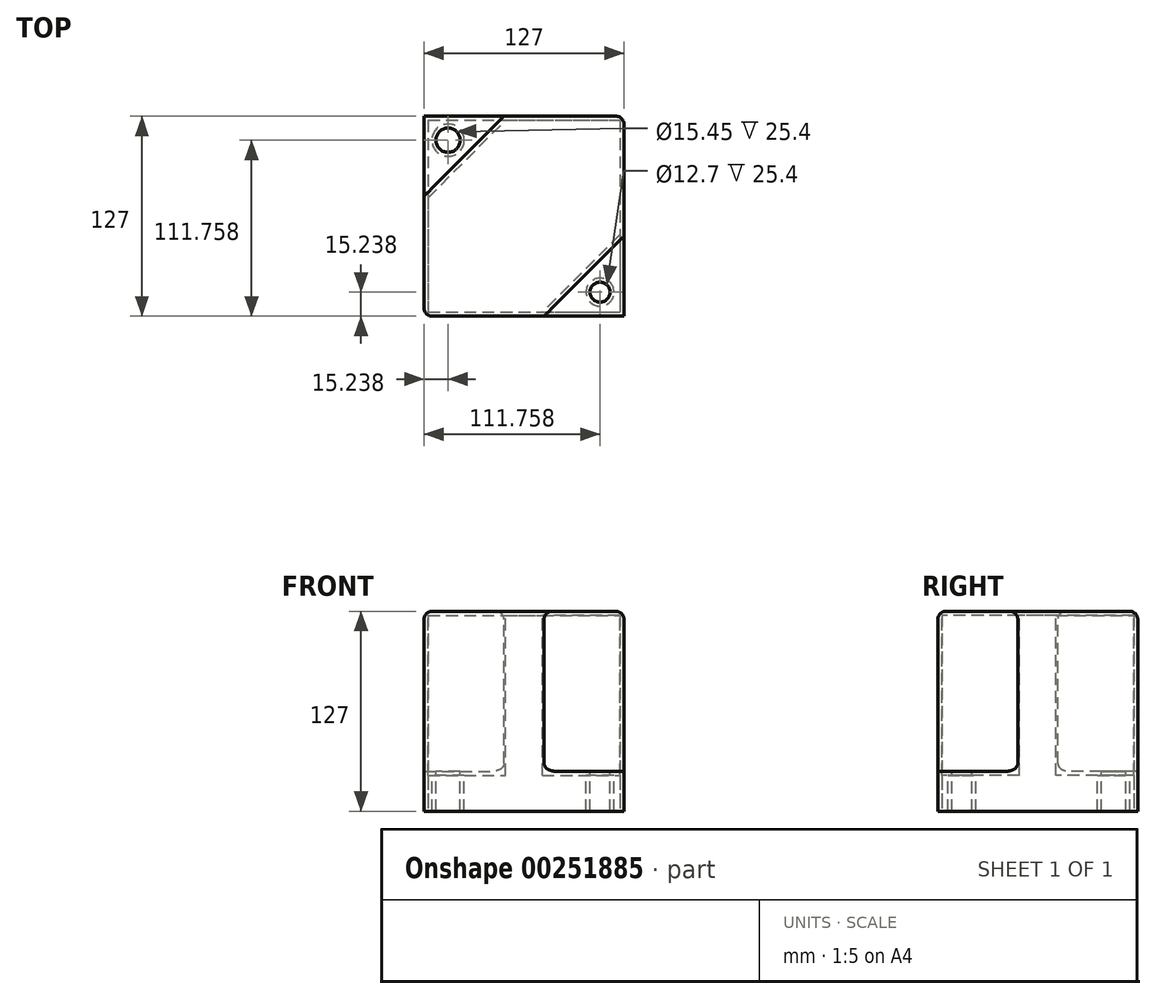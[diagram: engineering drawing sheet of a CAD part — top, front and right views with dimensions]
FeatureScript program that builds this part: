
annotation { "Feature Type Name" : "Feature", "Feature Type Description" : "" }
export const myFeature = defineFeature(function(context is Context, id is Id, definition is map)
    precondition{}
    {
        {
            var Q0;
            Q0=qCreatedBy(makeId("Top.planeOp"),FACE);
            var sketch = newSketch(context, id + "F0", { "sketchPlane" : qUnion([Q0])});
            skLineSegment(sketch, "E0.bottom", {"start": v(-61.38, 68.42) * mm, "end": v(65.62, 68.42) * mm});
            skLineSegment(sketch, "E0.top", {"start": v(-61.38, -58.58) * mm, "end": v(65.62, -58.58) * mm});
            skLineSegment(sketch, "E0.left", {"start": v(-61.38, 68.42) * mm, "end": v(-61.38, -58.58) * mm});
            skLineSegment(sketch, "E0.right", {"start": v(65.62, 68.42) * mm, "end": v(65.62, -58.58) * mm});
            skSolve(sketch);
        }
        {
            var Q0;
            Q0 = qSketchRegion(id + "F0", true);
            extrude(context, id + "F1", {"entities" : qUnion([Q0]), "depth" : 127 * mm});
        }
        {
            var Q0;
            Q0=makeQuery(id+"F1.opExtrude","CAP_FACE",FACE,{"disambiguationData":[OSD([sQuery(id+"F0.wireOp",EDGE,"E0.bottom"),sQuery(id+"F0.wireOp",EDGE,"E0.top"),sQuery(id+"F0.wireOp",EDGE,"E0.left"),sQuery(id+"F0.wireOp",EDGE,"E0.right")])],"isStart":false});
            var sketch = newSketch(context, id + "F2", { "sketchPlane" : qUnion([Q0])});
            skLineSegment(sketch, "E1", {"start": v(-61.38, 17.62) * mm, "end": v(-10.58, 68.42) * mm});
            skLineSegment(sketch, "E2", {"start": v(65.62, -7.78) * mm, "end": v(14.82, -58.58) * mm});
            skSolve(sketch);
        }
        {
            var Q0;
            {var subQ0=sQuery(id+"F2.wireOp",EDGE,"E1");Q0=makeQuery(id+"F2.imprint","IMPRINT",FACE,{"disambiguationData":[TD([[makeQuery(id+"F2.imprint","IMPRINT",EDGE,{"derivedFrom":subQ0}),1.0]])]});}
            var Q1;
            {var subQ0=sQuery(id+"F2.wireOp",EDGE,"E2");Q1=makeQuery(id+"F2.imprint","IMPRINT",FACE,{"disambiguationData":[TD([[makeQuery(id+"F2.imprint","IMPRINT",EDGE,{"derivedFrom":subQ0}),1.0]])]});}
            extrude(context, id + "F3", {"entities" : qUnion([Q0, Q1]), "operationType" : NewBodyOperationType.REMOVE, "oppositeDirection" : true, "depth" : 101.6 * mm});
        }
        {
            var Q0;
            Q0=makeQuery(id+"F3.boolean.opBoolean","COPY",FACE,{"derivedFrom":makeQuery(id+"F3.opExtrude","CAP_FACE",FACE,{"disambiguationData":[OSD([sQuery(id+"F0.wireOp",EDGE,"E0.bottom"),sQuery(id+"F0.wireOp",EDGE,"E0.left"),sQuery(id+"F2.wireOp",EDGE,"E1")])],"isStart":false})});
            var sketch = newSketch(context, id + "F4", { "sketchPlane" : qUnion([Q0])});
            skCircle(sketch, "E3", {"center": v(-46.14, 53.18) * mm, "radius": 7.73 * mm});
            skCircle(sketch, "E4", {"center": v(50.38, -43.34) * mm, "radius": 6.35 * mm});
            skSolve(sketch);
        }
        {
            var Q0;
            Q0=makeQuery(id+"F4.imprint","IMPRINT",FACE,{"disambiguationData":[TD([[makeQuery(id+"F4.imprint","IMPRINT",EDGE,{"derivedFrom":sQuery(id+"F4.wireOp",EDGE,"E4")}),1.0]])]});
            var Q1;
            Q1=makeQuery(id+"F4.imprint","IMPRINT",FACE,{"disambiguationData":[TD([[makeQuery(id+"F4.imprint","IMPRINT",EDGE,{"derivedFrom":sQuery(id+"F4.wireOp",EDGE,"E3")}),1.0]])]});
            extrude(context, id + "F5", {"entities" : qUnion([Q0, Q1]), "operationType" : NewBodyOperationType.REMOVE, "oppositeDirection" : true, "depth" : 203.2 * mm});
        }
        {
            var Q0;
            Q0=makeQuery(id+"F1.opExtrude","CAP_FACE",FACE,{"disambiguationData":[OSD([sQuery(id+"F0.wireOp",EDGE,"E0.bottom"),sQuery(id+"F0.wireOp",EDGE,"E0.top"),sQuery(id+"F0.wireOp",EDGE,"E0.left"),sQuery(id+"F0.wireOp",EDGE,"E0.right")])],"isStart":true});
            shell(context, id + "F6", {"entities" : qUnion([Q0]), "thickness" : 2.54 * mm});
        }
        {
            var Q0;
            Q0=makeQuery(id+"F1.opExtrude","CAP_EDGE",EDGE,{"disambiguationData":[OSD([sQuery(id+"F0.wireOp",EDGE,"E0.top")])],"isStart":false});
            var Q1;
            Q1=makeQuery(id+"F3.boolean.opBoolean","COPY",EDGE,{"derivedFrom":makeQuery(id+"F3.opExtrude","CAP_EDGE",EDGE,{"disambiguationData":[OSD([sQuery(id+"F2.wireOp",EDGE,"E2")])],"isStart":true})});
            var Q2;
            Q2=makeQuery(id+"F1.opExtrude","CAP_EDGE",EDGE,{"disambiguationData":[OSD([sQuery(id+"F0.wireOp",EDGE,"E0.right")])],"isStart":false});
            var Q3;
            Q3=makeQuery(id+"F1.opExtrude","CAP_EDGE",EDGE,{"disambiguationData":[OSD([sQuery(id+"F0.wireOp",EDGE,"E0.bottom")])],"isStart":false});
            var Q4;
            Q4=makeQuery(id+"F3.boolean.opBoolean","COPY",EDGE,{"derivedFrom":makeQuery(id+"F3.opExtrude","CAP_EDGE",EDGE,{"disambiguationData":[OSD([sQuery(id+"F2.wireOp",EDGE,"E1")])],"isStart":true})});
            var Q5;
            Q5=makeQuery(id+"F1.opExtrude","CAP_EDGE",EDGE,{"disambiguationData":[OSD([sQuery(id+"F0.wireOp",EDGE,"E0.left")])],"isStart":false});
            var Q6;
            Q6=makeQuery(id+"F3.boolean.opBoolean","COPY",EDGE,{"derivedFrom":makeQuery(id+"F3.opExtrude","CAP_EDGE",EDGE,{"disambiguationData":[OSD([sQuery(id+"F0.wireOp",EDGE,"E0.top")])],"isStart":false})});
            var Q7;
            Q7=makeQuery(id+"F3.boolean.opBoolean","COPY",EDGE,{"derivedFrom":makeQuery(id+"F3.opExtrude","CAP_EDGE",EDGE,{"disambiguationData":[OSD([sQuery(id+"F0.wireOp",EDGE,"E0.right")])],"isStart":false})});
            var Q8;
            Q8=makeQuery(id+"F3.boolean.opBoolean","COPY",EDGE,{"derivedFrom":makeQuery(id+"F3.opExtrude","CAP_EDGE",EDGE,{"disambiguationData":[OSD([sQuery(id+"F2.wireOp",EDGE,"E2")])],"isStart":false})});
            var Q9;
            Q9=makeQuery(id+"F1.opExtrude","SWEPT_EDGE",EDGE,{"disambiguationData":[OSD([sQuery(id+"F0.wireOp",EDGE,"E0.bottom"),sQuery(id+"F0.wireOp",EDGE,"E0.right")])]});
            var Q10;
            Q10=makeQuery(id+"F1.opExtrude","SWEPT_EDGE",EDGE,{"disambiguationData":[OSD([sQuery(id+"F0.wireOp",EDGE,"E0.top"),sQuery(id+"F0.wireOp",EDGE,"E0.left")])]});
            var Q11;
            Q11=makeQuery(id+"F3.boolean.opBoolean","COPY",EDGE,{"derivedFrom":makeQuery(id+"F3.opExtrude","SWEPT_EDGE",EDGE,{"disambiguationData":[OSD([sQuery(id+"F0.wireOp",EDGE,"E0.bottom"),sQuery(id+"F2.wireOp",EDGE,"E1")])]})});
            var Q12;
            Q12=makeQuery(id+"F3.boolean.opBoolean","COPY",EDGE,{"derivedFrom":makeQuery(id+"F3.opExtrude","CAP_EDGE",EDGE,{"disambiguationData":[OSD([sQuery(id+"F2.wireOp",EDGE,"E1")])],"isStart":false})});
            var Q13;
            Q13=makeQuery(id+"F3.boolean.opBoolean","COPY",EDGE,{"derivedFrom":makeQuery(id+"F3.opExtrude","CAP_EDGE",EDGE,{"disambiguationData":[OSD([sQuery(id+"F0.wireOp",EDGE,"E0.bottom")])],"isStart":false})});
            var Q14;
            Q14=makeQuery(id+"F3.boolean.opBoolean","COPY",EDGE,{"derivedFrom":makeQuery(id+"F3.opExtrude","CAP_EDGE",EDGE,{"disambiguationData":[OSD([sQuery(id+"F0.wireOp",EDGE,"E0.left")])],"isStart":false})});
            var Q15;
            Q15=makeQuery(id+"F3.boolean.opBoolean","COPY",EDGE,{"derivedFrom":makeQuery(id+"F3.opExtrude","SWEPT_EDGE",EDGE,{"disambiguationData":[OSD([sQuery(id+"F0.wireOp",EDGE,"E0.right"),sQuery(id+"F2.wireOp",EDGE,"E2")])]})});
            var Q16;
            Q16=makeQuery(id+"F3.boolean.opBoolean","COPY",EDGE,{"derivedFrom":makeQuery(id+"F3.opExtrude","SWEPT_EDGE",EDGE,{"disambiguationData":[OSD([sQuery(id+"F0.wireOp",EDGE,"E0.top"),sQuery(id+"F2.wireOp",EDGE,"E2")])]})});
            var Q17;
            Q17=makeQuery(id+"F3.boolean.opBoolean","COPY",EDGE,{"derivedFrom":makeQuery(id+"F3.opExtrude","SWEPT_EDGE",EDGE,{"disambiguationData":[OSD([sQuery(id+"F0.wireOp",EDGE,"E0.left"),sQuery(id+"F2.wireOp",EDGE,"E1")])]})});
            fillet(context, id + "F7", {"entities" : qUnion([Q0, Q1, Q2, Q3, Q4, Q5, Q6, Q7, Q8, Q9, Q10, Q11, Q12, Q13, Q14, Q15, Q16, Q17]), "radius" : 5.08 * mm, "tangentPropagation" : true, "allowEdgeOverflow" : false});
        }
    });
